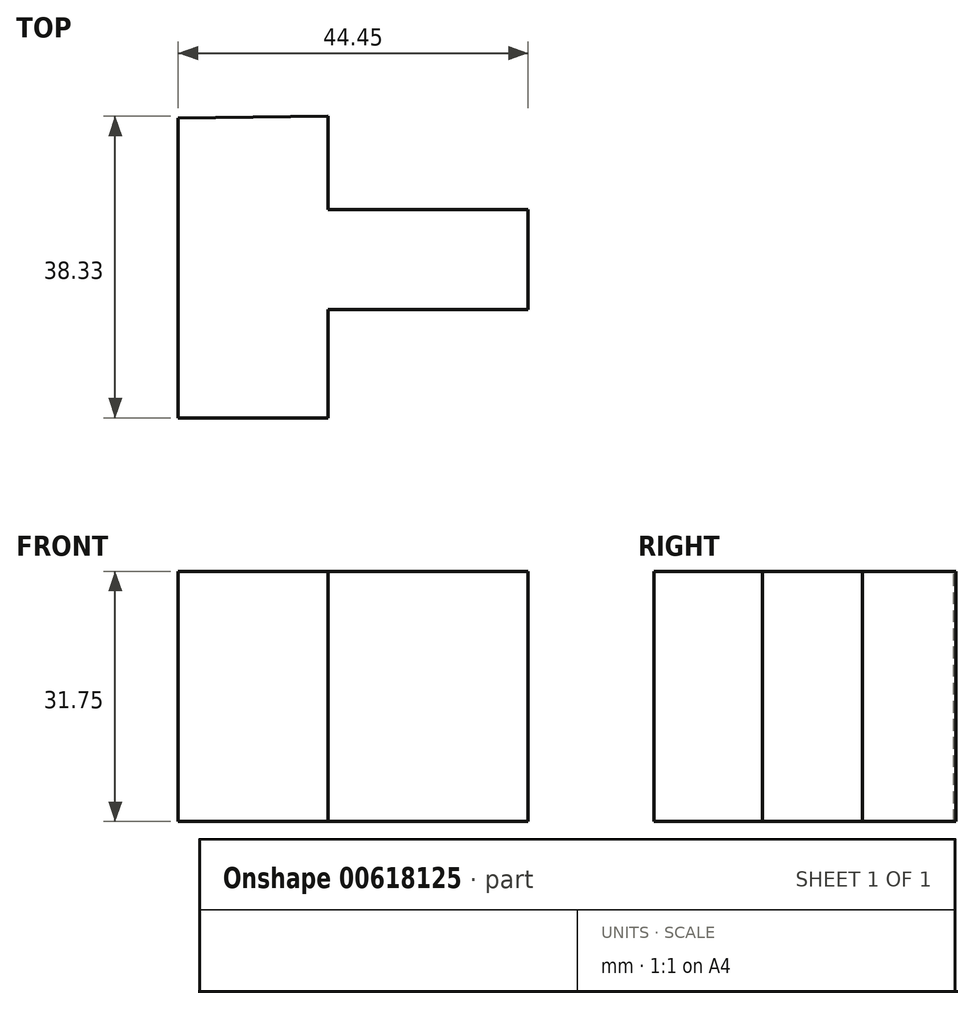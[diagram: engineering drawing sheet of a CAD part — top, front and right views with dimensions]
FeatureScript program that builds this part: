
annotation { "Feature Type Name" : "Feature", "Feature Type Description" : "" }
export const myFeature = defineFeature(function(context is Context, id is Id, definition is map)
    precondition{}
    {
        {
            var Q0;
            Q0=qCreatedBy(makeId("Top.planeOp"),FACE);
            var sketch = newSketch(context, id + "F0", { "sketchPlane" : qUnion([Q0])});
            skLineSegment(sketch, "E0", {"start": v(0, 38.1) * mm, "end": v(0, 0) * mm});
            skLineSegment(sketch, "E1", {"start": v(0, 0) * mm, "end": v(19.05, 0) * mm});
            skLineSegment(sketch, "E2", {"start": v(19.05, 0) * mm, "end": v(19.05, 13.78) * mm});
            skLineSegment(sketch, "E3", {"start": v(19.05, 13.78) * mm, "end": v(44.45, 13.78) * mm});
            skLineSegment(sketch, "E4", {"start": v(44.45, 13.78) * mm, "end": v(44.45, 26.48) * mm});
            skLineSegment(sketch, "E5", {"start": v(44.45, 26.48) * mm, "end": v(19.05, 26.48) * mm});
            skLineSegment(sketch, "E6", {"start": v(19.05, 26.48) * mm, "end": v(19.05, 38.33) * mm});
            skLineSegment(sketch, "E7", {"start": v(19.05, 38.33) * mm, "end": v(0, 38.1) * mm});
            skSolve(sketch);
        }
        {
            var Q0;
            Q0=makeQuery(id+"F0.imprint","IMPRINT",FACE,{"disambiguationData":[TD([[makeQuery(id+"F0.imprint","IMPRINT",EDGE,{"derivedFrom":sQuery(id+"F0.wireOp",EDGE,"E0")}),1.0]])]});
            extrude(context, id + "F1", {"entities" : qUnion([Q0]), "oppositeDirection" : true, "depth" : 31.75 * mm, "offsetDistance" : 25.4 * mm});
        }
    });
